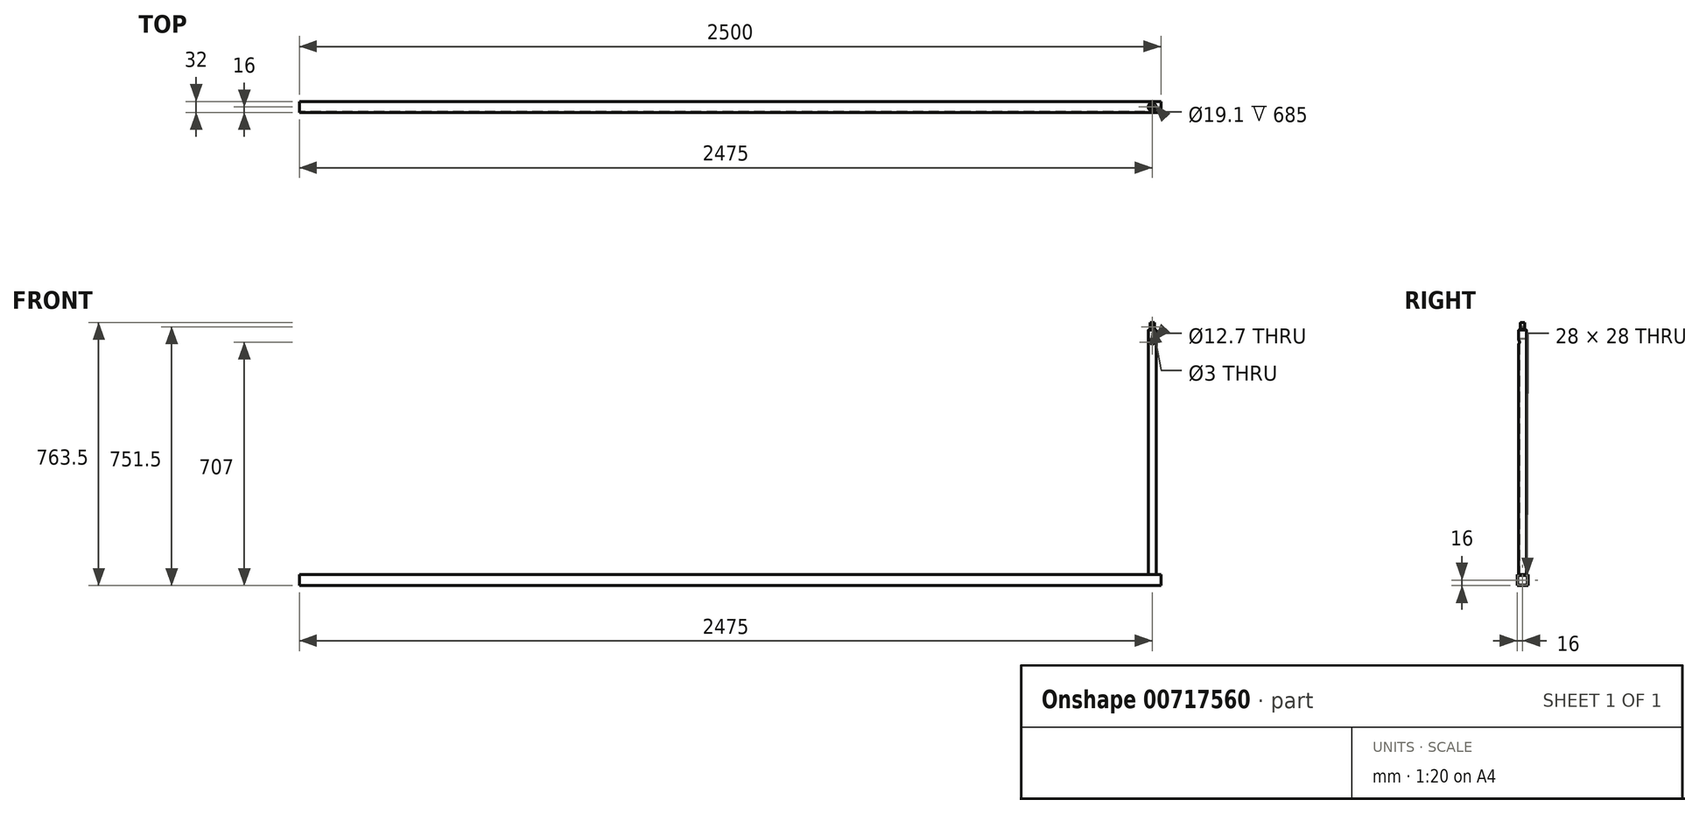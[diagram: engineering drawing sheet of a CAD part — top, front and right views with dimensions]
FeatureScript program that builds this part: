
annotation { "Feature Type Name" : "Feature", "Feature Type Description" : "" }
export const myFeature = defineFeature(function(context is Context, id is Id, definition is map)
    precondition{}
    {
        {
            var Q0;
            Q0=qCreatedBy(makeId("Right.planeOp"),FACE);
            var sketch = newSketch(context, id + "F0", { "sketchPlane" : qUnion([Q0])});
            skLineSegment(sketch, "E0.bottom", {"start": v(-16, 16) * mm, "end": v(16, 16) * mm});
            skLineSegment(sketch, "E0.top", {"start": v(-16, -16) * mm, "end": v(16, -16) * mm});
            skLineSegment(sketch, "E0.left", {"start": v(-16, 16) * mm, "end": v(-16, -16) * mm});
            skLineSegment(sketch, "E0.right", {"start": v(16, 16) * mm, "end": v(16, -16) * mm});
            skLineSegment(sketch, "E1.0", {"start": v(14, 14) * mm, "end": v(14, -14) * mm});
            skLineSegment(sketch, "E1.1", {"start": v(-14, 14) * mm, "end": v(14, 14) * mm});
            skLineSegment(sketch, "E1.2", {"start": v(-14, 14) * mm, "end": v(-14, -14) * mm});
            skLineSegment(sketch, "E1.3", {"start": v(-14, -14) * mm, "end": v(14, -14) * mm});
            skSolve(sketch);
        }
        {
            var Q0;
            Q0 = qSketchRegion(id + "F0", true);
            extrude(context, id + "F1", {"entities" : qUnion([Q0]), "depth" : 25 * mm, "offsetDistance" : 25 * mm});
        }
        {
            var Q0;
            Q0 = qSketchRegion(id + "F0", true);
            extrude(context, id + "F2", {"entities" : qUnion([Q0]), "operationType" : NewBodyOperationType.ADD, "oppositeDirection" : true, "depth" : 2475 * mm, "offsetDistance" : 25 * mm});
        }
        {
            var Q0;
            {var subQ0=sQuery(id+"F0.wireOp",EDGE,"E0.bottom");Q0=makeQuery(id+"F2.boolean.opBoolean","MERGE",FACE,{"derivedFrom":[makeQuery(id+"F1.opExtrude","SWEPT_FACE",FACE,{"disambiguationData":[OSD([subQ0])]}),makeQuery(id+"F2.opExtrude","SWEPT_FACE",FACE,{"disambiguationData":[OSD([subQ0])]})]});}
            var sketch = newSketch(context, id + "F3", { "sketchPlane" : qUnion([Q0])});
            skCircle(sketch, "E2", {"center": v(0, 0) * mm, "radius": 11.55 * mm});
            skCircle(sketch, "E3", {"center": v(0, 0) * mm, "radius": 9.55 * mm});
            skSolve(sketch);
        }
        {
            var Q0;
            Q0 = qSketchRegion(id + "F3", true);
            extrude(context, id + "F4", {"entities" : qUnion([Q0]), "operationType" : NewBodyOperationType.ADD, "depth" : 710 * mm, "offsetDistance" : 25 * mm});
        }
        {
            var Q0;
            Q0=makeQuery(id+"F4.opExtrude","CAP_FACE",FACE,{"disambiguationData":[OSD([sQuery(id+"F3.wireOp",EDGE,"E2"),sQuery(id+"F3.wireOp",EDGE,"E3")])],"isStart":false});
            var sketch = newSketch(context, id + "F5", { "sketchPlane" : qUnion([Q0])});
            skCircle(sketch, "E4.0", {"center": v(0, 0) * mm, "radius": 9.55 * mm});
            skSolve(sketch);
        }
        {
            var Q0;
            Q0 = qSketchRegion(id + "F5", true);
            extrude(context, id + "F6", {"entities" : qUnion([Q0]), "oppositeDirection" : true, "depth" : 25 * mm, "offsetDistance" : 25 * mm});
        }
        {
            var Q0;
            Q0=makeQuery(id+"F6.opExtrude","CAP_FACE",FACE,{"disambiguationData":[OSD([sQuery(id+"F5.wireOp",EDGE,"E4.0")])],"isStart":true});
            var sketch = newSketch(context, id + "F7", { "sketchPlane" : qUnion([Q0])});
            skCircle(sketch, "E5", {"center": v(0, 0) * mm, "radius": 6.35 * mm});
            skSolve(sketch);
        }
        {
            var Q0;
            Q0 = qSketchRegion(id + "F7", true);
            extrude(context, id + "F8", {"entities" : qUnion([Q0]), "operationType" : NewBodyOperationType.ADD, "depth" : 21.5 * mm, "offsetDistance" : 25 * mm});
        }
        {
            var Q0;
            Q0=qCreatedBy(makeId("Front.planeOp"),FACE);
            var sketch = newSketch(context, id + "F9", { "sketchPlane" : qUnion([Q0])});
            skCircle(sketch, "E6", {"center": v(0, 735.5) * mm, "radius": 1.5 * mm});
            skSolve(sketch);
        }
        {
            var Q0;
            Q0 = qSketchRegion(id + "F9", true);
            extrude(context, id + "F10", {"entities" : qUnion([Q0]), "operationType" : NewBodyOperationType.REMOVE, "endBound" : BoundingType.SYMMETRIC, "depth" : 13 * mm, "offsetDistance" : 25 * mm});
        }
        {
            var Q0;
            Q0=makeQuery(id+"F6.opExtrude","CAP_FACE",FACE,{"disambiguationData":[OSD([sQuery(id+"F5.wireOp",EDGE,"E4.0")])],"isStart":true});
            var sketch = newSketch(context, id + "F11", { "sketchPlane" : qUnion([Q0])});
            skCircle(sketch, "E7.0", {"center": v(0, 0) * mm, "radius": 6.35 * mm});
            skCircle(sketch, "E8.0", {"center": v(0, 0) * mm, "radius": 9.55 * mm});
            skSolve(sketch);
        }
        {
            var Q0;
            Q0 = qSketchRegion(id + "F11", true);
            extrude(context, id + "F12", {"entities" : qUnion([Q0]), "operationType" : NewBodyOperationType.ADD, "depth" : 2 * mm, "offsetDistance" : 25 * mm});
        }
        {
            var Q0;
            Q0=qCreatedBy(makeId("Front.planeOp"),FACE);
            var sketch = newSketch(context, id + "F13", { "sketchPlane" : qUnion([Q0])});
            skLineSegment(sketch, "E9", {"start": v(0, 721.34) * mm, "end": v(0, 660.08) * mm, "construction": true});
            skCircle(sketch, "E10", {"center": v(0, 691) * mm, "radius": 6.35 * mm});
            skSolve(sketch);
        }
        {
            var Q0;
            Q0 = qSketchRegion(id + "F13", true);
            extrude(context, id + "F14", {"entities" : qUnion([Q0]), "operationType" : NewBodyOperationType.REMOVE, "depth" : 25 * mm, "offsetDistance" : 25 * mm});
        }
    });
